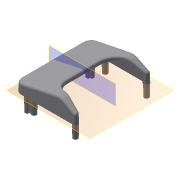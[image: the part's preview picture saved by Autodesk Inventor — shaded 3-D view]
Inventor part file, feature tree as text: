
AUTODESK INVENTOR PART (.ipt)
format: ipt  version: 2016 (Build 200138000, 138)  size: 700,416 bytes
history: native  units: mm
features: extrude x10, sketch x10, projected_geometry x8, fillet x7, reference x3, plane x2, shell x1, mirror x1
ambient origin geometry x8: Origin, YZ Plane, XZ Plane, XY Plane, X Axis, Y Axis, Z Axis, Center Point
bodies: Solid1 (feature_tree)
feature tree (42):
  plane  "Work Plane1"
  extrude  "Extrusion1"  Depth=7.0mm
  fillet  "Fillet1"  Radius=3.0mm
  plane  "Work Plane2"
  extrude  "Extrusion2"  Depth=5.0mm
  fillet  "Fillet2"  Radius=1.0mm
  fillet  "Fillet3"  Radius=1.5mm
  shell  "Shell1"  Thickness=3.05mm
  extrude  "Extrusion3"  Depth=60.0mm
  fillet  "Fillet4"  Radius=1.0mm
  extrude  "Extrusion4"  Depth=3.08mm
  extrude  "Extrusion5"  TaperAngle=15.0deg  [1 undecoded]
  fillet  "Fillet5"  [1 undecoded]
  fillet  "Fillet6"  Radius=10.0mm
  extrude  "Extrusion6"  Depth=5.0mm
  extrude  "Extrusion7"  Depth=0.349066mm TaperAngle=0.0deg
  extrude  "Extrusion8"  Depth=2.0mm
  extrude  "Extrusion9"  Depth=2.0mm
  extrude  "Extrusion11"  Depth=0.174533mm TaperAngle=0.0deg
  mirror  "Mirror3"
  fillet  "Fillet11"  Radius=5.0mm
  sketch  "Sketch1"  dims[d1=1.0mm d2=7.0mm d3=-0.349066mm d4=3.0mm]
  reference  "Reference1"
  sketch  "Sketch2"  dims[d5=60.0mm d6=0.0mm d7=5.0mm d8=1.0mm d9=1.5mm d10=3.05mm]
  sketch  "Sketch3"  dims[d11=3.05mm d12=60.0mm d13=0.174533mm d14=1.0mm]
  projected_geometry  "Projected Loop1"
  sketch  "Sketch4"  dims[d15=3.08mm d16=3.08mm]
  projected_geometry  "Projected Loop2"
  sketch  "Sketch5"  dims[d17=7.0mm d18=-0.087266mm d19=15.0deg d20=15.0deg d21=10.0mm]
  projected_geometry  "Projected Loop3"
  sketch  "Sketch6"  dims[d22=10.0mm d23=0.349066mm d24=5.0mm]
  projected_geometry  "Projected Loop4"
  sketch  "Sketch7"  dims[d25=0.7mm d27=0.0mm d28=0.349066mm]
  projected_geometry  "Projected Loop5"
  sketch  "Sketch8"  dims[d29=5.0mm d30=-0.174533mm d31=2.0mm]
  reference  "Reference2"
  reference  "Reference3"
  sketch  "Sketch9"  dims[d32=16.6mm d33=2.0mm]
  projected_geometry  "Projected Loop6"
  sketch  "Sketch11"  dims[d34=0.0mm d35=0.0mm d36=0.174533mm d37=5.0mm d38=-0.174533mm d54=1.5mm d57=1.5mm d58=10.0mm d59=-0.174533mm d60=0.65mm d61=0.65mm d62=0.65mm d63=0.65mm d64=0.65mm d65=0.65mm d66=0.65mm d67=0.65mm d70=0.4mm d71=24.3mm]
  projected_geometry  "Projected Loop7"
  projected_geometry  "Projected Loop8"
note: 2 required parameter values undecoded (feature->parameter linkage not recoverable at this tier; creation-order binding heuristic only, values carry confidence <= 0.55)
